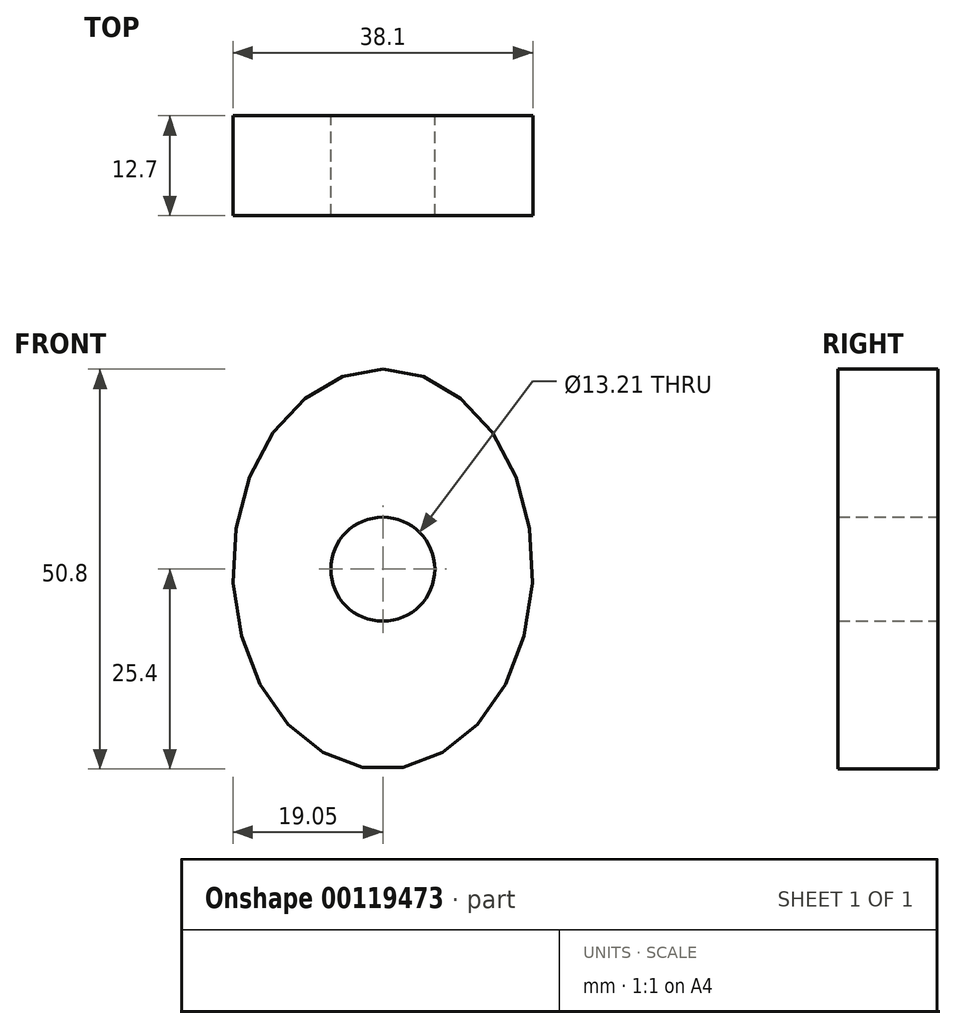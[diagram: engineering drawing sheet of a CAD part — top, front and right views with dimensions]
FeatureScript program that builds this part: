
annotation { "Feature Type Name" : "Feature", "Feature Type Description" : "" }
export const myFeature = defineFeature(function(context is Context, id is Id, definition is map)
    precondition{}
    {
        {
            var Q0;
            Q0=qCreatedBy(makeId("Front.planeOp"),FACE);
            var sketch = newSketch(context, id + "F0", { "sketchPlane" : qUnion([Q0])});
            skEllipse(sketch, "E0", {"center": v(0, 0) * mm, "majorRadius": 25.4 * mm, "minorRadius": 19.05 * mm, "majorAxis": v(0, 1)});
            skSolve(sketch);
        }
        {
            var Q0;
            Q0=makeQuery(id+"F0.imprint","IMPRINT",FACE,{"disambiguationData":[TD([[makeQuery(id+"F0.imprint","IMPRINT",EDGE,{"derivedFrom":sQuery(id+"F0.wireOp",EDGE,"E0")}),1.0]])]});
            extrude(context, id + "F1", {"entities" : qUnion([Q0]), "depth" : 12.7 * mm});
        }
        {
            var Q0;
            Q0=makeQuery(id+"F1.opExtrude","CAP_FACE",FACE,{"disambiguationData":[OSD([sQuery(id+"F0.wireOp",EDGE,"E0")])],"isStart":false});
            var sketch = newSketch(context, id + "F2", { "sketchPlane" : qUnion([Q0])});
            skCircle(sketch, "E1", {"center": v(0, 0) * mm, "radius": 6.6 * mm});
            skSolve(sketch);
        }
        {
            var Q0;
            Q0=makeQuery(id+"F2.imprint","IMPRINT",FACE,{"disambiguationData":[TD([[makeQuery(id+"F2.imprint","IMPRINT",EDGE,{"derivedFrom":sQuery(id+"F2.wireOp",EDGE,"E1")}),1.0]])]});
            var Q1;
            Q1=sQuery(id+"F2.wireOp",EDGE,"E1");
            extrude(context, id + "F3", {"entities" : qUnion([Q0]), "operationType" : NewBodyOperationType.REMOVE, "surfaceEntities" : qUnion([Q1]), "endBound" : BoundingType.SYMMETRIC, "depth" : 25.4 * mm});
        }
    });
